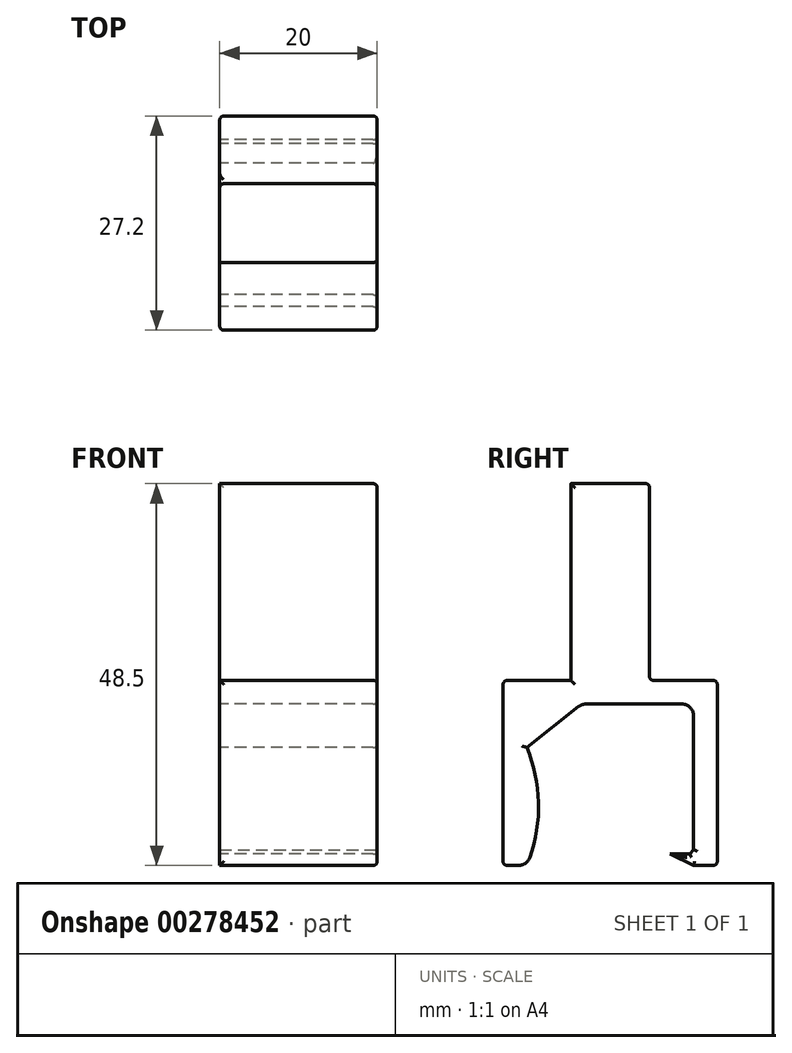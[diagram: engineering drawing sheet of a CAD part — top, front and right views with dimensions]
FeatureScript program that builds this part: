
annotation { "Feature Type Name" : "Feature", "Feature Type Description" : "" }
export const myFeature = defineFeature(function(context is Context, id is Id, definition is map)
    precondition{}
    {
        {
            var Q0;
            Q0=qCreatedBy(makeId("Right.planeOp"),FACE);
            var sketch = newSketch(context, id + "F0", { "sketchPlane" : qUnion([Q0])});
            skLineSegment(sketch, "E0", {"start": v(0, 0) * mm, "end": v(3, 0) * mm});
            skLineSegment(sketch, "E1", {"start": v(3, 0) * mm, "end": v(3, 19) * mm});
            skLineSegment(sketch, "E2", {"start": v(3, 19) * mm, "end": v(-18.2, 19) * mm});
            skLineSegment(sketch, "E3", {"start": v(-18.2, 19) * mm, "end": v(-18.2, -1.5) * mm});
            skLineSegment(sketch, "E4", {"start": v(0, 0) * mm, "end": v(3, -1.5) * mm});
            skLineSegment(sketch, "E5", {"start": v(3, -1.5) * mm, "end": v(3, 0) * mm});
            skLineSegment(sketch, "E6.0", {"start": v(-21.2, 22) * mm, "end": v(-21.2, -1.5) * mm});
            skLineSegment(sketch, "E6.1", {"start": v(6, 22) * mm, "end": v(-21.2, 22) * mm});
            skLineSegment(sketch, "E7", {"start": v(-21.2, -1.5) * mm, "end": v(-18.2, -1.5) * mm});
            skLineSegment(sketch, "E8", {"start": v(3, -1.5) * mm, "end": v(6, -1.5) * mm});
            skLineSegment(sketch, "E9", {"start": v(6, 22) * mm, "end": v(6, -1.5) * mm});
            skLineSegment(sketch, "E10", {"start": v(-7.6, 22) * mm, "end": v(-7.6, 47) * mm, "construction": true});
            skLineSegment(sketch, "E11.bottom", {"start": v(-2.6, 22) * mm, "end": v(-12.6, 22) * mm});
            skLineSegment(sketch, "E11.top", {"start": v(-2.6, 47) * mm, "end": v(-12.6, 47) * mm});
            skLineSegment(sketch, "E11.left", {"start": v(-2.6, 22) * mm, "end": v(-2.6, 47) * mm});
            skLineSegment(sketch, "E11.right", {"start": v(-12.6, 22) * mm, "end": v(-12.6, 47) * mm});
            skPoint(sketch, "E11.middle", {"position": v(-7.6, 34.5) * mm});
            skPoint(sketch, "E12", {"position": v(-11.2, 22) * mm});
            skLineSegment(sketch, "E13", {"start": v(-11.2, 22) * mm, "end": v(-11.2, 19) * mm, "construction": true});
            skPoint(sketch, "E14", {"position": v(-18.2, 13.5) * mm});
            skLineSegment(sketch, "E15", {"start": v(-11.2, 19) * mm, "end": v(-18.2, 13.5) * mm});
            skArc(sketch, "E16", {"start": v(-18.2, -1.5) * mm, "mid": v(-16.7, 6) * mm, "end": v(-18.2, 13.5) * mm});
            skLineSegment(sketch, "E17", {"start": v(-36.2, 6) * mm, "end": v(-1.56, 6) * mm, "construction": true});
            skSolve(sketch);
        }
        {
            var Q0;
            Q0 = qSketchRegion(id + "F0", true);
            extrude(context, id + "F1", {"entities" : qUnion([Q0]), "depth" : 20 * mm});
        }
        {
            var Q0;
            Q0=makeQuery(id+"F1.opExtrude","SWEPT_EDGE",EDGE,{"disambiguationData":[OSD([sQuery(id+"F0.wireOp",EDGE,"E0"),sQuery(id+"F0.wireOp",EDGE,"E1"),sQuery(id+"F0.wireOp",EDGE,"E5")])]});
            chamfer(context, id + "F2", {"entities" : qUnion([Q0]), "width" : 0.5 * mm, "tangentPropagation" : true});
        }
        {
            var Q0;
            Q0=makeQuery(id+"F1.opExtrude","SWEPT_EDGE",EDGE,{"disambiguationData":[OSD([sQuery(id+"F0.wireOp",EDGE,"E1"),sQuery(id+"F0.wireOp",EDGE,"E2")])]});
            var Q1;
            Q1=makeQuery(id+"F1.opExtrude","SWEPT_EDGE",EDGE,{"disambiguationData":[OSD([sQuery(id+"F0.wireOp",EDGE,"E2"),sQuery(id+"F0.wireOp",EDGE,"E3")])]});
            var Q2;
            Q2=makeQuery(id+"F1.opExtrude","SWEPT_EDGE",EDGE,{"disambiguationData":[OSD([sQuery(id+"F0.wireOp",EDGE,"E3"),sQuery(id+"F0.wireOp",EDGE,"E7")])]});
            fillet(context, id + "F3", {"entities" : qUnion([Q0, Q1, Q2]), "radius" : 1.5 * mm, "tangentPropagation" : true, "allowEdgeOverflow" : false});
        }
        {
            var Q0;
            Q0=makeQuery(id+"F1.opExtrude","SWEPT_FACE",FACE,{"disambiguationData":[OSD([sQuery(id+"F0.wireOp",EDGE,"E6.0")])]});
            var Q1;
            Q1=makeQuery(id+"F1.opExtrude","CAP_FACE",FACE,{"disambiguationData":[OSD([sQuery(id+"F0.wireOp",EDGE,"E0"),sQuery(id+"F0.wireOp",EDGE,"E1"),sQuery(id+"F0.wireOp",EDGE,"E2"),sQuery(id+"F0.wireOp",EDGE,"E4"),sQuery(id+"F0.wireOp",EDGE,"E6.0"),sQuery(id+"F0.wireOp",EDGE,"E6.1"),sQuery(id+"F0.wireOp",EDGE,"E7"),sQuery(id+"F0.wireOp",EDGE,"E8"),sQuery(id+"F0.wireOp",EDGE,"E9"),sQuery(id+"F0.wireOp",EDGE,"E11.top"),sQuery(id+"F0.wireOp",EDGE,"E11.left"),sQuery(id+"F0.wireOp",EDGE,"E11.right"),sQuery(id+"F0.wireOp",EDGE,"E15"),sQuery(id+"F0.wireOp",EDGE,"E16")])],"isStart":false});
            var Q2;
            Q2=makeQuery(id+"F1.opExtrude","SWEPT_FACE",FACE,{"disambiguationData":[OSD([sQuery(id+"F0.wireOp",EDGE,"E9")])]});
            var Q3;
            Q3=makeQuery(id+"F1.opExtrude","SWEPT_FACE",FACE,{"disambiguationData":[OSD([sQuery(id+"F0.wireOp",EDGE,"E11.left")])]});
            fillet(context, id + "F4", {"entities" : qUnion([Q0, Q1, Q2, Q3]), "radius" : 0.5 * mm, "tangentPropagation" : true, "allowEdgeOverflow" : false});
        }
    });
